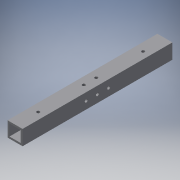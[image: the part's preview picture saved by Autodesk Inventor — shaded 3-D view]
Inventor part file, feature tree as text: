
AUTODESK INVENTOR PART (.ipt)
format: ipt  version: 2018 (Build 220112000, 112)  size: 168,960 bytes
history: native  units: in
note: dims shown in document units (in); Inventor stores cm internally (conversion verified against a paired STEP export)
features: extrude x6, sketch x6, projected_geometry x2
ambient origin geometry x8: Origin, YZ Plane, XZ Plane, XY Plane, X Axis, Y Axis, Z Axis, Center Point
bodies: Solid1 (feature_tree)
feature tree (14):
  extrude  "Extrusion1"  Depth=1.0in
  extrude  "Extrusion2"  Depth=0.125in TaperAngle=0.0deg
  extrude  "Extrusion3"  Depth=0.5in
  extrude  "Extrusion4"  Depth=0.2031in
  extrude  "Extrusion5"  Depth=0.5in TaperAngle=0.0deg
  extrude  "Extrusion6"  Depth=1.0in TaperAngle=0.0deg
  sketch  "Sketch1"  dims[d0=1.0in d1=1.0in]
  sketch  "Sketch2"  dims[d2=0.125in d3=7.5in d4=0.0in]
  sketch  "Sketch3"  dims[d6=0.5in d7=0.5in]
  projected_geometry  "Projected Loop1"
  sketch  "Sketch4"  dims[d8=0.2031in d9=0.2031in]
  projected_geometry  "Projected Loop2"
  sketch  "Sketch5"  dims[d10=6.0in d11=0.0in d12=0.5in d13=0.0in]
  sketch  "Sketch6"  dims[d14=1.0in d15=0.0in d16=1.0in d17=0.0in d18=4.585in d19=4.585in d20=0.2031in d21=0.2031in d22=2.0in d23=0.0in d24=0.5in d25=0.75in d26=0.75in d27=0.2031in d28=0.2031in d29=0.2031in d30=1.0in d31=0.0in]
